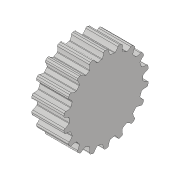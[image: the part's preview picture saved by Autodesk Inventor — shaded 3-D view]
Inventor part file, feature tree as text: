
AUTODESK INVENTOR PART (.ipt)
format: ipt  version: 2019.4 (Build 234330000, 330)  size: 235,008 bytes
history: native  units: mm
features: fillet x2, other x1, extrude x1, pattern_circular x1, sketch x1
ambient origin geometry x8: Origin, YZ Plane, XZ Plane, XY Plane, X Axis, Y Axis, Z Axis, Center Point
bodies: Body1 (feature_tree)
feature tree (6):
  other  "ソリッド1"
  extrude  "押し出し1"  Depth=1.95mm
  fillet  "フィレット1"  Radius=1.975mm
  fillet  "フィレット2"  Radius=1.11mm
  pattern_circular  "円形状パターン1"  [2 undecoded]
  sketch  "スケッチ1"
note: 2 required parameter values undecoded (feature->parameter linkage not recoverable at this tier; creation-order binding heuristic only, values carry confidence <= 0.55)
